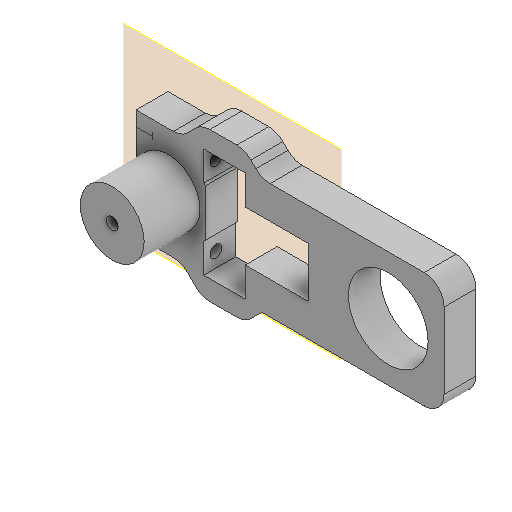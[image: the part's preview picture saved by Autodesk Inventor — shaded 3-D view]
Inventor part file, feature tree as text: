
AUTODESK INVENTOR PART (.ipt)
format: ipt  version: 2022 (Build 260153000, 153)  size: 276,992 bytes
history: native  units: mm
features: reference x7, other x7, sketch x5, extrude x4, plane x1, hole x1, mirror x1, fillet x1, projected_geometry x1
ambient origin geometry x8: Origin, YZ Plane, XZ Plane, XY Plane, X Axis, Y Axis, Z Axis, Center Point
bodies: Volumenkörper1 (feature_tree)
feature tree (28):
  plane  "Arbeitsebene1"
  extrude  "Extrusion1"  Depth=5.0mm
  hole  "Bohrung1"  [1 undecoded]
  mirror  "Spiegeln2"
  extrude  "Extrusion5"  Depth=8.0mm TaperAngle=0.0deg
  extrude  "Extrusion6"  TaperAngle=135.0deg  [1 undecoded]
  extrude  "Extrusion7"  Depth=14.0mm TaperAngle=0.0deg
  fillet  "Rundung1"  Radius=12.0mm
  sketch  "Skizze1"  dims[d0=0.2mm d2=5.0mm]
  reference  "Referenz1"
  sketch  "Skizze2"  dims[d4=17.0mm d7=0.5mm]
  reference  "Referenz6"
  projected_geometry  "Projizierte Kontur1"
  reference  "Referenz8"
  reference  "Referenz9"
  sketch  "Skizze6"  dims[d8=3.5mm d9=8.0mm d10=0.0mm]
  sketch  "Skizze7"  dims[d11=3.0mm]
  sketch  "Skizze8"  dims[d12=3.0mm d13=6.0mm d14=6.0mm d15=4.0mm d16=90.0deg d17=20.0mm d18=20.594885mm d21=135.0deg d32=14.0mm d33=0.0mm d34=12.0mm d35=20.0mm d36=0.0mm d37=3.0mm d38=15.0mm d39=0.0mm d44=5.0mm d45=20.0mm d46=14.0mm d47=20.0mm d48=14.5mm]
  reference  "Referenz14"
  reference  "Referenz15"
  reference  "Referenz16"
  other  "Assembly_Cube_Z-Stage_NEMA8_captive_v0.iam"
  other  "00_MGN12H, LINEAR GUIDE BLOCK:1"
  other  "Assembly_Cube_Z_Focus_MGN_NEMA_belt_pushing_v3.iam"
  other  "30_Cube_Z_Focus_MGN_NEMA_adapter_RMS:1"
  other  "00_Joy-IT-B20SHD4353_NEMA8_captive:1"
  other  "Baugruppe5"
  other  "30_Cube_Z_Focus_MGN_NEMA_base_belt_pushing_v3:1"
note: 2 required parameter values undecoded (feature->parameter linkage not recoverable at this tier; creation-order binding heuristic only, values carry confidence <= 0.55)
